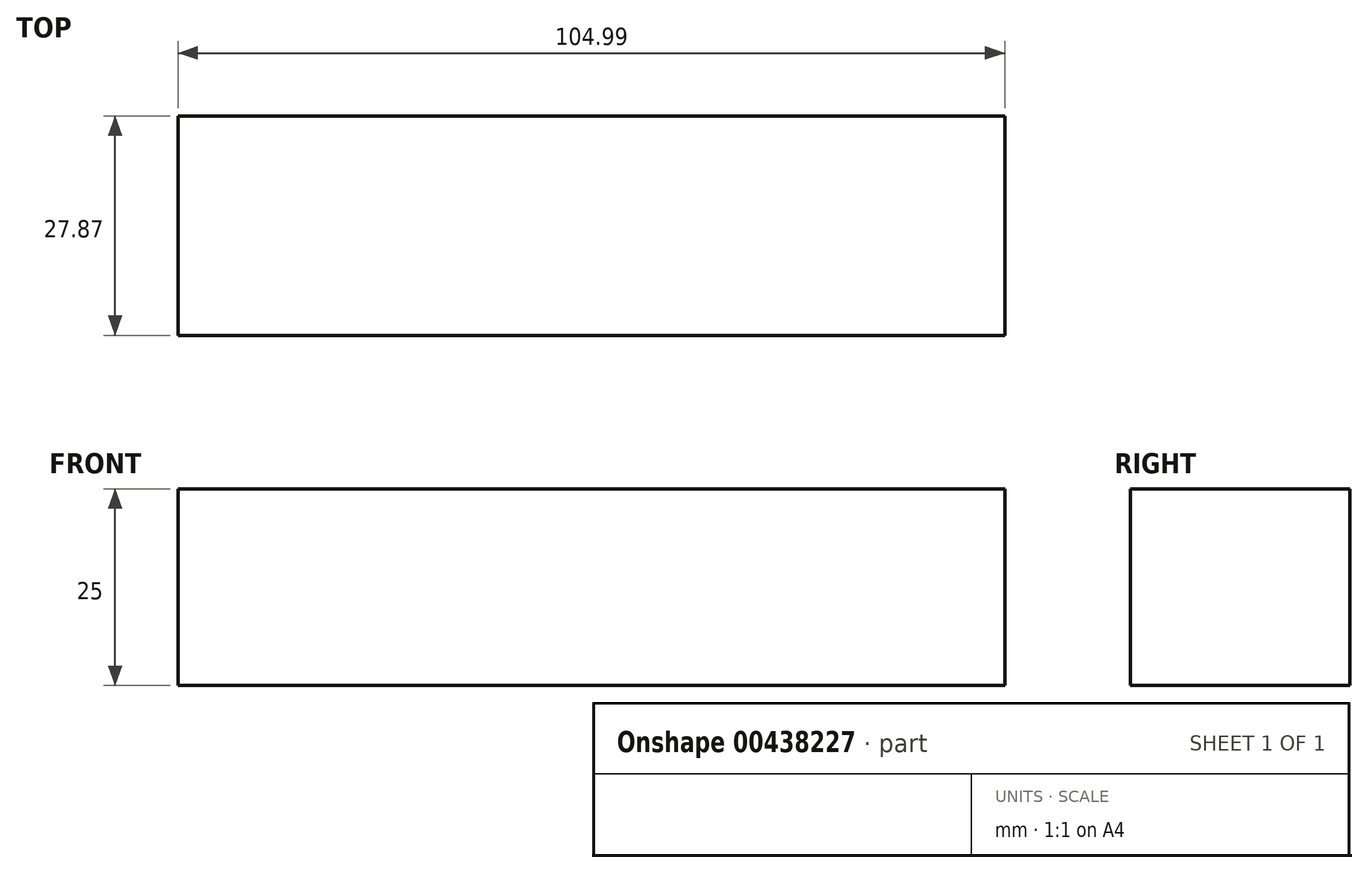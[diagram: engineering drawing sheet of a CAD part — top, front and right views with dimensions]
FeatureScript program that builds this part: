
annotation { "Feature Type Name" : "Feature", "Feature Type Description" : "" }
export const myFeature = defineFeature(function(context is Context, id is Id, definition is map)
    precondition{}
    {
        {
            var Q0;
            Q0=qCreatedBy(makeId("Top.planeOp"),FACE);
            cPlane(context, id + "F0", {"entities" : qUnion([Q0]), "cplaneType" : CPlaneType.OFFSET, "offset" : 0 * mm, "width" : 150 * mm, "height" : 150 * mm});
        }
        {
            var Q0;
            Q0=qCreatedBy(id+"F0.planeOp",FACE);
            var sketch = newSketch(context, id + "F1", { "sketchPlane" : qUnion([Q0])});
            skLineSegment(sketch, "E0.bottom", {"start": v(-58.78, 5.84) * mm, "end": v(46.2, 5.84) * mm});
            skLineSegment(sketch, "E0.top", {"start": v(-58.78, -22.03) * mm, "end": v(46.2, -22.03) * mm});
            skLineSegment(sketch, "E0.left", {"start": v(-58.78, 5.84) * mm, "end": v(-58.78, -22.03) * mm});
            skLineSegment(sketch, "E0.right", {"start": v(46.2, 5.84) * mm, "end": v(46.2, -22.03) * mm});
            skSolve(sketch);
        }
        {
            var Q0;
            Q0 = qSketchRegion(id + "F1", true);
            extrude(context, id + "F2", {"entities" : qUnion([Q0]), "depth" : 25 * mm});
        }
    });
